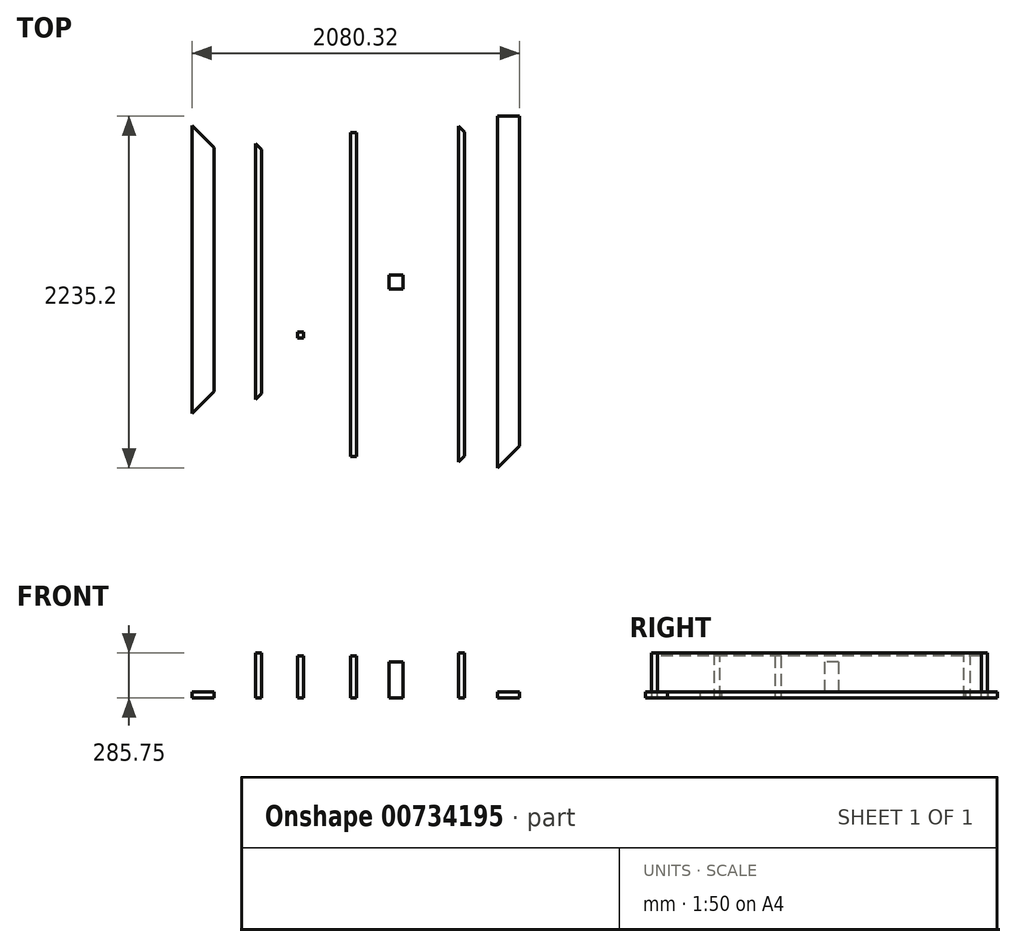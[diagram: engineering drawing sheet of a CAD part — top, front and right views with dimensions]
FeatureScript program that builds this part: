
annotation { "Feature Type Name" : "Feature", "Feature Type Description" : "" }
export const myFeature = defineFeature(function(context is Context, id is Id, definition is map)
    precondition{}
    {
        {
            var Q0;
            Q0=qCreatedBy(makeId("Top.planeOp"),FACE);
            var sketch = newSketch(context, id + "F0", { "sketchPlane" : qUnion([Q0])});
            skLineSegment(sketch, "E0.bottom", {"start": v(19.05, -1037.58) * mm, "end": v(-19.05, -1037.58) * mm});
            skLineSegment(sketch, "E0.top", {"start": v(19.05, 1096.02) * mm, "end": v(-19.05, 1096.02) * mm});
            skLineSegment(sketch, "E0.left", {"start": v(19.05, -1037.58) * mm, "end": v(19.05, 1096.02) * mm});
            skLineSegment(sketch, "E0.right", {"start": v(-19.05, -1037.58) * mm, "end": v(-19.05, 1096.02) * mm});
            skPoint(sketch, "E0.middle", {"position": v(0, 29.22) * mm});
            skSolve(sketch);
        }
        {
            var Q0;
            Q0=makeQuery(id+"F0.imprint","IMPRINT",FACE,{"disambiguationData":[TD([[makeQuery(id+"F0.imprint","IMPRINT",EDGE,{"derivedFrom":sQuery(id+"F0.wireOp",EDGE,"E0.bottom")}),-1.0]])]});
            extrude(context, id + "F1", {"entities" : qUnion([Q0]), "depth" : 285.75 * mm, "offsetDistance" : 25.4 * mm});
        }
        {
            var Q0;
            Q0=qCreatedBy(makeId("Top.planeOp"),FACE);
            var sketch = newSketch(context, id + "F2", { "sketchPlane" : qUnion([Q0])});
            skLineSegment(sketch, "E1.bottom", {"start": v(-1308.24, 986.63) * mm, "end": v(-1270.14, 986.63) * mm});
            skLineSegment(sketch, "E1.top", {"start": v(-1308.24, -638.97) * mm, "end": v(-1270.14, -638.97) * mm});
            skLineSegment(sketch, "E1.left", {"start": v(-1308.24, 986.63) * mm, "end": v(-1308.24, -638.97) * mm});
            skLineSegment(sketch, "E1.right", {"start": v(-1270.14, 986.63) * mm, "end": v(-1270.14, -638.97) * mm});
            skSolve(sketch);
        }
        {
            var Q0;
            Q0=makeQuery(id+"F2.imprint","IMPRINT",FACE,{"disambiguationData":[TD([[makeQuery(id+"F2.imprint","IMPRINT",EDGE,{"derivedFrom":sQuery(id+"F2.wireOp",EDGE,"E1.bottom")}),-1.0]])]});
            extrude(context, id + "F3", {"entities" : qUnion([Q0]), "depth" : 285.75 * mm, "offsetDistance" : 25.4 * mm});
        }
        {
            var Q0;
            Q0=qCreatedBy(makeId("Top.planeOp"),FACE);
            var sketch = newSketch(context, id + "F4", { "sketchPlane" : qUnion([Q0])});
            skLineSegment(sketch, "E2.bottom", {"start": v(-704.89, 1055.07) * mm, "end": v(-666.79, 1055.07) * mm});
            skLineSegment(sketch, "E2.top", {"start": v(-704.89, -1002.33) * mm, "end": v(-666.79, -1002.33) * mm});
            skLineSegment(sketch, "E2.left", {"start": v(-704.89, 1055.07) * mm, "end": v(-704.89, -1002.33) * mm});
            skLineSegment(sketch, "E2.right", {"start": v(-666.79, 1055.07) * mm, "end": v(-666.79, -1002.33) * mm});
            skSolve(sketch);
        }
        {
            var Q0;
            Q0=makeQuery(id+"F4.imprint","IMPRINT",FACE,{"disambiguationData":[TD([[makeQuery(id+"F4.imprint","IMPRINT",EDGE,{"derivedFrom":sQuery(id+"F4.wireOp",EDGE,"E2.bottom")}),-1.0]])]});
            extrude(context, id + "F5", {"entities" : qUnion([Q0]), "depth" : 266.7 * mm, "offsetDistance" : 25.4 * mm});
        }
        {
            var Q0;
            Q0=qCreatedBy(makeId("Top.planeOp"),FACE);
            var sketch = newSketch(context, id + "F6", { "sketchPlane" : qUnion([Q0])});
            skLineSegment(sketch, "E3.bottom", {"start": v(-1042.75, -212.58) * mm, "end": v(-1004.65, -212.58) * mm});
            skLineSegment(sketch, "E3.top", {"start": v(-1042.75, -250.68) * mm, "end": v(-1004.65, -250.68) * mm});
            skLineSegment(sketch, "E3.left", {"start": v(-1042.75, -212.58) * mm, "end": v(-1042.75, -250.68) * mm});
            skLineSegment(sketch, "E3.right", {"start": v(-1004.65, -212.58) * mm, "end": v(-1004.65, -250.68) * mm});
            skSolve(sketch);
        }
        {
            var Q0;
            Q0=makeQuery(id+"F6.imprint","IMPRINT",FACE,{"disambiguationData":[TD([[makeQuery(id+"F6.imprint","IMPRINT",EDGE,{"derivedFrom":sQuery(id+"F6.wireOp",EDGE,"E3.bottom")}),-1.0]])]});
            extrude(context, id + "F7", {"entities" : qUnion([Q0]), "depth" : 266.7 * mm, "offsetDistance" : 25.4 * mm});
        }
        {
            var Q0;
            Q0=qCreatedBy(makeId("Top.planeOp"),FACE);
            var sketch = newSketch(context, id + "F8", { "sketchPlane" : qUnion([Q0])});
            skLineSegment(sketch, "E4.bottom", {"start": v(-460.84, 151.6) * mm, "end": v(-371.94, 151.6) * mm});
            skLineSegment(sketch, "E4.top", {"start": v(-460.84, 62.7) * mm, "end": v(-371.94, 62.7) * mm});
            skLineSegment(sketch, "E4.left", {"start": v(-460.84, 151.6) * mm, "end": v(-460.84, 62.7) * mm});
            skLineSegment(sketch, "E4.right", {"start": v(-371.94, 151.6) * mm, "end": v(-371.94, 62.7) * mm});
            skSolve(sketch);
        }
        {
            var Q0;
            Q0=makeQuery(id+"F8.imprint","IMPRINT",FACE,{"disambiguationData":[TD([[makeQuery(id+"F8.imprint","IMPRINT",EDGE,{"derivedFrom":sQuery(id+"F8.wireOp",EDGE,"E4.bottom")}),-1.0]])]});
            extrude(context, id + "F9", {"entities" : qUnion([Q0]), "depth" : 228.6 * mm, "offsetDistance" : 25.4 * mm});
        }
        {
            var Q0;
            Q0=qCreatedBy(makeId("Top.planeOp"),FACE);
            var sketch = newSketch(context, id + "F10", { "sketchPlane" : qUnion([Q0])});
            skLineSegment(sketch, "E5.bottom", {"start": v(368.03, 1160.95) * mm, "end": v(228.33, 1160.95) * mm});
            skLineSegment(sketch, "E5.top", {"start": v(368.03, -1074.25) * mm, "end": v(228.33, -1074.25) * mm});
            skLineSegment(sketch, "E5.left", {"start": v(368.03, 1160.95) * mm, "end": v(368.03, -1074.25) * mm});
            skLineSegment(sketch, "E5.right", {"start": v(228.33, 1160.95) * mm, "end": v(228.33, -1074.25) * mm});
            skSolve(sketch);
        }
        {
            var Q0;
            Q0 = qSketchRegion(id + "F10", true);
            extrude(context, id + "F11", {"entities" : qUnion([Q0]), "depth" : 38.1 * mm, "offsetDistance" : 25.4 * mm});
        }
        {
            var Q0;
            Q0=qCreatedBy(makeId("Top.planeOp"),FACE);
            var sketch = newSketch(context, id + "F12", { "sketchPlane" : qUnion([Q0])});
            skLineSegment(sketch, "E6.bottom", {"start": v(-1712.3, 1099.1) * mm, "end": v(-1572.6, 1099.1) * mm});
            skLineSegment(sketch, "E6.top", {"start": v(-1712.3, -729.7) * mm, "end": v(-1572.6, -729.7) * mm});
            skLineSegment(sketch, "E6.left", {"start": v(-1712.3, 1099.1) * mm, "end": v(-1712.3, -729.7) * mm});
            skLineSegment(sketch, "E6.right", {"start": v(-1572.6, 1099.1) * mm, "end": v(-1572.6, -729.7) * mm});
            skSolve(sketch);
        }
        {
            var Q0;
            Q0=makeQuery(id+"F12.imprint","IMPRINT",FACE,{"disambiguationData":[TD([[makeQuery(id+"F12.imprint","IMPRINT",EDGE,{"derivedFrom":sQuery(id+"F12.wireOp",EDGE,"E6.bottom")}),-1.0]])]});
            extrude(context, id + "F13", {"entities" : qUnion([Q0]), "depth" : 38.1 * mm, "offsetDistance" : 25.4 * mm});
        }
        {
            var Q0;
            Q0=makeQuery(id+"F1.opExtrude","CAP_FACE",FACE,{"disambiguationData":[OSD([sQuery(id+"F0.wireOp",EDGE,"E0.bottom"),sQuery(id+"F0.wireOp",EDGE,"E0.top"),sQuery(id+"F0.wireOp",EDGE,"E0.left"),sQuery(id+"F0.wireOp",EDGE,"E0.right")])],"isStart":false});
            var sketch = newSketch(context, id + "F14", { "sketchPlane" : qUnion([Q0])});
            skLineSegment(sketch, "E7", {"start": v(-19.05, -1037.58) * mm, "end": v(19.05, -1037.58) * mm});
            skLineSegment(sketch, "E8", {"start": v(19.05, -1037.58) * mm, "end": v(19.05, -999.48) * mm});
            skLineSegment(sketch, "E9", {"start": v(19.05, -999.48) * mm, "end": v(-19.05, -1037.58) * mm});
            skLineSegment(sketch, "E10", {"start": v(19.05, 1096.02) * mm, "end": v(-19.05, 1096.02) * mm});
            skLineSegment(sketch, "E11", {"start": v(-19.05, 1096.02) * mm, "end": v(19.05, 1057.92) * mm});
            skLineSegment(sketch, "E12", {"start": v(19.05, 1057.92) * mm, "end": v(19.05, 1096.02) * mm});
            skSolve(sketch);
        }
        {
            var Q0;
            Q0 = qSketchRegion(id + "F14", true);
            extrude(context, id + "F15", {"entities" : qUnion([Q0]), "operationType" : NewBodyOperationType.REMOVE, "endBound" : BoundingType.THROUGH_ALL, "oppositeDirection" : true, "depth" : 25.4 * mm, "offsetDistance" : 25.4 * mm});
        }
        {
            var Q0;
            Q0=makeQuery(id+"F3.opExtrude","CAP_FACE",FACE,{"disambiguationData":[OSD([sQuery(id+"F2.wireOp",EDGE,"E1.bottom"),sQuery(id+"F2.wireOp",EDGE,"E1.top"),sQuery(id+"F2.wireOp",EDGE,"E1.left"),sQuery(id+"F2.wireOp",EDGE,"E1.right")])],"isStart":false});
            var sketch = newSketch(context, id + "F16", { "sketchPlane" : qUnion([Q0])});
            skLineSegment(sketch, "E13", {"start": v(-1308.24, 986.63) * mm, "end": v(-1270.14, 986.63) * mm});
            skLineSegment(sketch, "E14", {"start": v(-1270.14, 986.63) * mm, "end": v(-1270.14, 948.53) * mm});
            skLineSegment(sketch, "E15", {"start": v(-1270.14, 948.53) * mm, "end": v(-1308.24, 986.63) * mm});
            skLineSegment(sketch, "E16", {"start": v(-1270.14, -638.97) * mm, "end": v(-1308.24, -638.97) * mm});
            skLineSegment(sketch, "E17", {"start": v(-1308.24, -638.97) * mm, "end": v(-1270.14, -600.87) * mm});
            skLineSegment(sketch, "E18", {"start": v(-1270.14, -600.87) * mm, "end": v(-1270.14, -638.97) * mm});
            skSolve(sketch);
        }
        {
            var Q0;
            Q0 = qSketchRegion(id + "F16", true);
            extrude(context, id + "F17", {"entities" : qUnion([Q0]), "operationType" : NewBodyOperationType.REMOVE, "endBound" : BoundingType.THROUGH_ALL, "oppositeDirection" : true, "depth" : 25.4 * mm, "offsetDistance" : 25.4 * mm});
        }
        {
            var Q0;
            Q0=makeQuery(id+"F11.opExtrude","CAP_FACE",FACE,{"disambiguationData":[OSD([sQuery(id+"F10.wireOp",EDGE,"E5.bottom"),sQuery(id+"F10.wireOp",EDGE,"E5.top"),sQuery(id+"F10.wireOp",EDGE,"E5.left"),sQuery(id+"F10.wireOp",EDGE,"E5.right")])],"isStart":false});
            var sketch = newSketch(context, id + "F18", { "sketchPlane" : qUnion([Q0])});
            skLineSegment(sketch, "E19", {"start": v(228.33, -1074.25) * mm, "end": v(368.03, -1074.25) * mm});
            skLineSegment(sketch, "E20", {"start": v(368.03, -1074.25) * mm, "end": v(368.03, -934.55) * mm});
            skLineSegment(sketch, "E21", {"start": v(368.03, -934.55) * mm, "end": v(228.33, -1074.25) * mm});
            skSolve(sketch);
        }
        {
            var Q0;
            Q0 = qSketchRegion(id + "F18", true);
            extrude(context, id + "F19", {"entities" : qUnion([Q0]), "operationType" : NewBodyOperationType.REMOVE, "endBound" : BoundingType.THROUGH_ALL, "oppositeDirection" : true, "depth" : 25.4 * mm, "offsetDistance" : 25.4 * mm});
        }
        {
            var Q0;
            Q0=makeQuery(id+"F13.opExtrude","CAP_FACE",FACE,{"disambiguationData":[OSD([sQuery(id+"F12.wireOp",EDGE,"E6.bottom"),sQuery(id+"F12.wireOp",EDGE,"E6.top"),sQuery(id+"F12.wireOp",EDGE,"E6.left"),sQuery(id+"F12.wireOp",EDGE,"E6.right")])],"isStart":false});
            var sketch = newSketch(context, id + "F20", { "sketchPlane" : qUnion([Q0])});
            skLineSegment(sketch, "E22", {"start": v(-1712.3, 1099.1) * mm, "end": v(-1572.6, 1099.1) * mm});
            skLineSegment(sketch, "E23", {"start": v(-1572.6, 1099.1) * mm, "end": v(-1572.6, 959.4) * mm});
            skLineSegment(sketch, "E24", {"start": v(-1572.6, 959.4) * mm, "end": v(-1712.3, 1099.1) * mm});
            skLineSegment(sketch, "E25", {"start": v(-1712.3, -729.7) * mm, "end": v(-1572.6, -729.7) * mm});
            skLineSegment(sketch, "E26", {"start": v(-1572.6, -729.7) * mm, "end": v(-1572.6, -590) * mm});
            skLineSegment(sketch, "E27", {"start": v(-1572.6, -590) * mm, "end": v(-1712.3, -729.7) * mm});
            skSolve(sketch);
        }
        {
            var Q0;
            Q0 = qSketchRegion(id + "F20", true);
            extrude(context, id + "F21", {"entities" : qUnion([Q0]), "operationType" : NewBodyOperationType.REMOVE, "endBound" : BoundingType.THROUGH_ALL, "oppositeDirection" : true, "depth" : 25.4 * mm, "offsetDistance" : 25.4 * mm});
        }
    });
